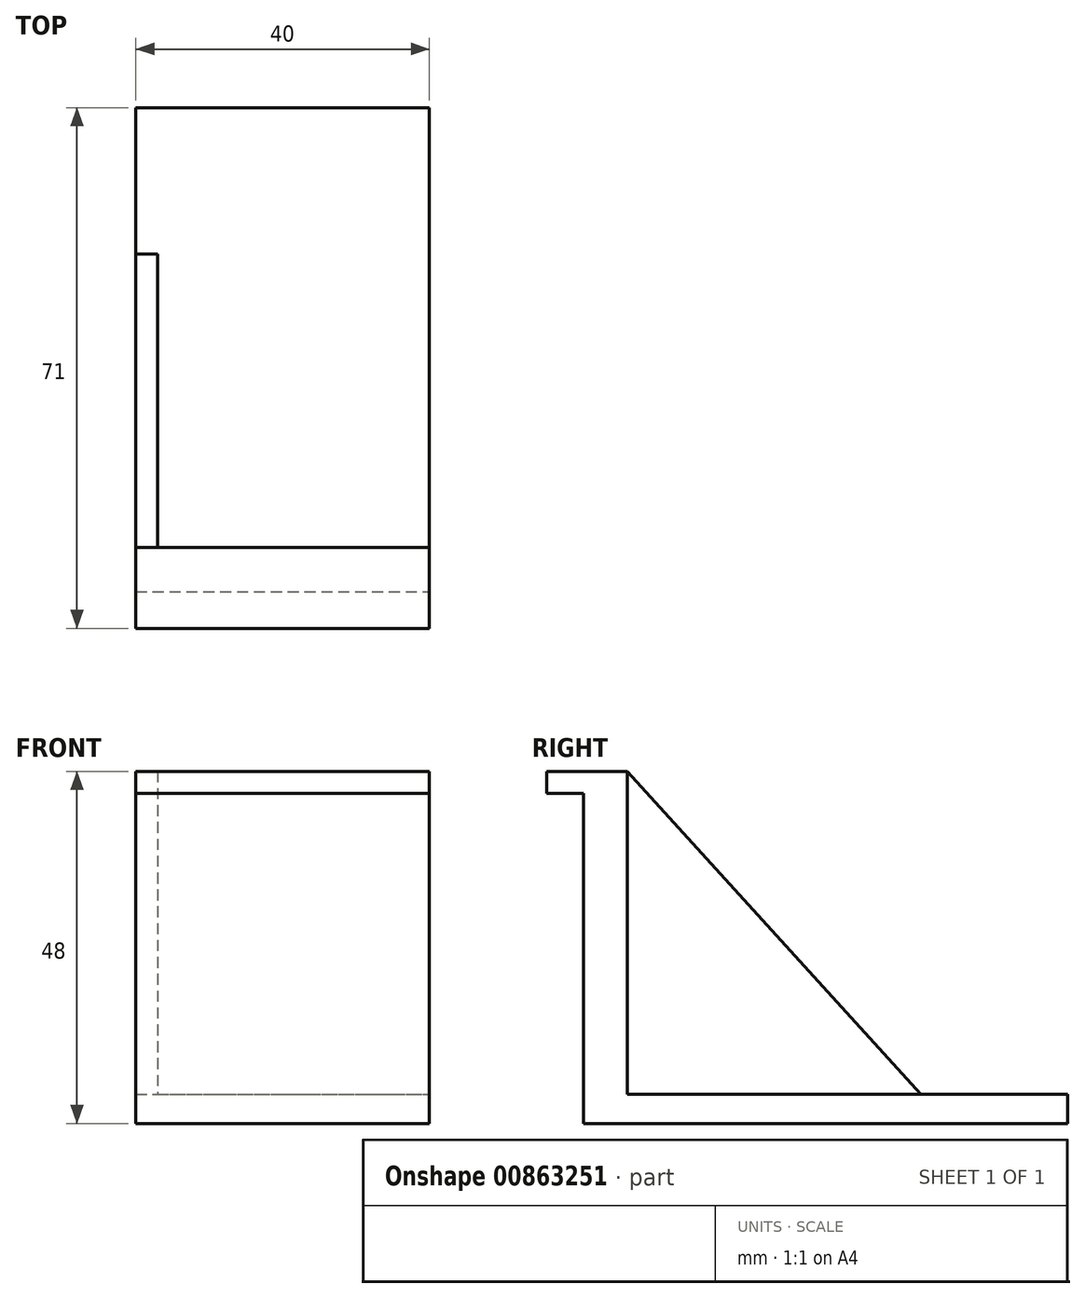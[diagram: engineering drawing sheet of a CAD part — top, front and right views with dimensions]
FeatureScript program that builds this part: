
annotation { "Feature Type Name" : "Feature", "Feature Type Description" : "" }
export const myFeature = defineFeature(function(context is Context, id is Id, definition is map)
    precondition{}
    {
        {
            var Q0;
            Q0=qCreatedBy(makeId("Top.planeOp"),FACE);
            var sketch = newSketch(context, id + "F0", { "sketchPlane" : qUnion([Q0])});
            skLineSegment(sketch, "E0.bottom", {"start": v(0, 0) * mm, "end": v(40, 0) * mm});
            skLineSegment(sketch, "E0.top", {"start": v(0, 6) * mm, "end": v(40, 6) * mm});
            skLineSegment(sketch, "E0.left", {"start": v(0, 0) * mm, "end": v(0, 6) * mm});
            skLineSegment(sketch, "E0.right", {"start": v(40, 0) * mm, "end": v(40, 6) * mm});
            skLineSegment(sketch, "E1.top", {"start": v(0, 46) * mm, "end": v(40, 46) * mm});
            skLineSegment(sketch, "E1.left", {"start": v(0, 6) * mm, "end": v(0, 46) * mm});
            skLineSegment(sketch, "E1.right", {"start": v(40, 6) * mm, "end": v(40, 46) * mm});
            skSolve(sketch);
        }
        {
            var Q0;
            Q0=makeQuery(id+"F0.imprint","IMPRINT",FACE,{"disambiguationData":[TD([[makeQuery(id+"F0.imprint","IMPRINT",EDGE,{"derivedFrom":sQuery(id+"F0.wireOp",EDGE,"E0.top")}),1.0]])]});
            extrude(context, id + "F1", {"entities" : qUnion([Q0]), "depth" : 4 * mm, "offsetDistance" : 25 * mm});
        }
        {
            var Q0;
            Q0=makeQuery(id+"F0.imprint","IMPRINT",FACE,{"disambiguationData":[TD([[makeQuery(id+"F0.imprint","IMPRINT",EDGE,{"derivedFrom":sQuery(id+"F0.wireOp",EDGE,"E0.bottom")}),1.0]])]});
            extrude(context, id + "F2", {"entities" : qUnion([Q0]), "operationType" : NewBodyOperationType.ADD, "depth" : 48 * mm, "offsetDistance" : 25 * mm});
        }
        {
            var Q0;
            Q0=makeQuery(id+"F2.opExtrude","SWEPT_FACE",FACE,{"disambiguationData":[OSD([sQuery(id+"F0.wireOp",EDGE,"E0.bottom")])]});
            var sketch = newSketch(context, id + "F3", { "sketchPlane" : qUnion([Q0])});
            skLineSegment(sketch, "E2", {"start": v(0, 48) * mm, "end": v(0, 45) * mm});
            skLineSegment(sketch, "E3", {"start": v(0, 45) * mm, "end": v(40, 45) * mm});
            skLineSegment(sketch, "E4", {"start": v(40, 45) * mm, "end": v(40, 48) * mm});
            skLineSegment(sketch, "E5", {"start": v(40, 48) * mm, "end": v(0, 48) * mm});
            skSolve(sketch);
        }
        {
            var Q0;
            Q0=makeQuery(id+"F3.imprint","IMPRINT",FACE,{"disambiguationData":[TD([[makeQuery(id+"F3.imprint","IMPRINT",EDGE,{"derivedFrom":sQuery(id+"F3.wireOp",EDGE,"E2")}),1.0]])]});
            extrude(context, id + "F4", {"entities" : qUnion([Q0]), "operationType" : NewBodyOperationType.ADD, "depth" : 5 * mm, "offsetDistance" : 25 * mm});
        }
        {
            var Q0;
            Q0=makeQuery(id+"F4.boolean.opBoolean","MERGE",FACE,{"derivedFrom":[makeQuery(id+"F2.boolean.opBoolean","MERGE",FACE,{"derivedFrom":[makeQuery(id+"F1.opExtrude","SWEPT_FACE",FACE,{"disambiguationData":[OSD([sQuery(id+"F0.wireOp",EDGE,"E1.left")])]}),makeQuery(id+"F2.opExtrude","SWEPT_FACE",FACE,{"disambiguationData":[OSD([sQuery(id+"F0.wireOp",EDGE,"E0.left")])]})]}),makeQuery(id+"F4.opExtrude","SWEPT_FACE",FACE,{"disambiguationData":[OSD([sQuery(id+"F3.wireOp",EDGE,"E2")])]})]});
            var sketch = newSketch(context, id + "F5", { "sketchPlane" : qUnion([Q0])});
            skLineSegment(sketch, "E6", {"start": v(-46, 4) * mm, "end": v(-6, 48) * mm});
            skLineSegment(sketch, "E7", {"start": v(-6, 48) * mm, "end": v(-6, 4) * mm});
            skLineSegment(sketch, "E8", {"start": v(-6, 4) * mm, "end": v(-46, 4) * mm});
            skSolve(sketch);
        }
        {
            var Q0;
            Q0=makeQuery(id+"F5.imprint","IMPRINT",FACE,{"disambiguationData":[TD([[makeQuery(id+"F5.imprint","IMPRINT",EDGE,{"derivedFrom":sQuery(id+"F5.wireOp",EDGE,"E6")}),-1.0]])]});
            extrude(context, id + "F6", {"entities" : qUnion([Q0]), "operationType" : NewBodyOperationType.ADD, "oppositeDirection" : true, "depth" : 3 * mm, "offsetDistance" : 25 * mm});
        }
        {
            var Q0;
            Q0=makeQuery(id+"F1.opExtrude","SWEPT_FACE",FACE,{"disambiguationData":[OSD([sQuery(id+"F0.wireOp",EDGE,"E1.top")])]});
            extrude(context, id + "F7", {"entities" : qUnion([Q0]), "operationType" : NewBodyOperationType.ADD, "depth" : 20 * mm, "offsetDistance" : 25 * mm});
        }
    });
